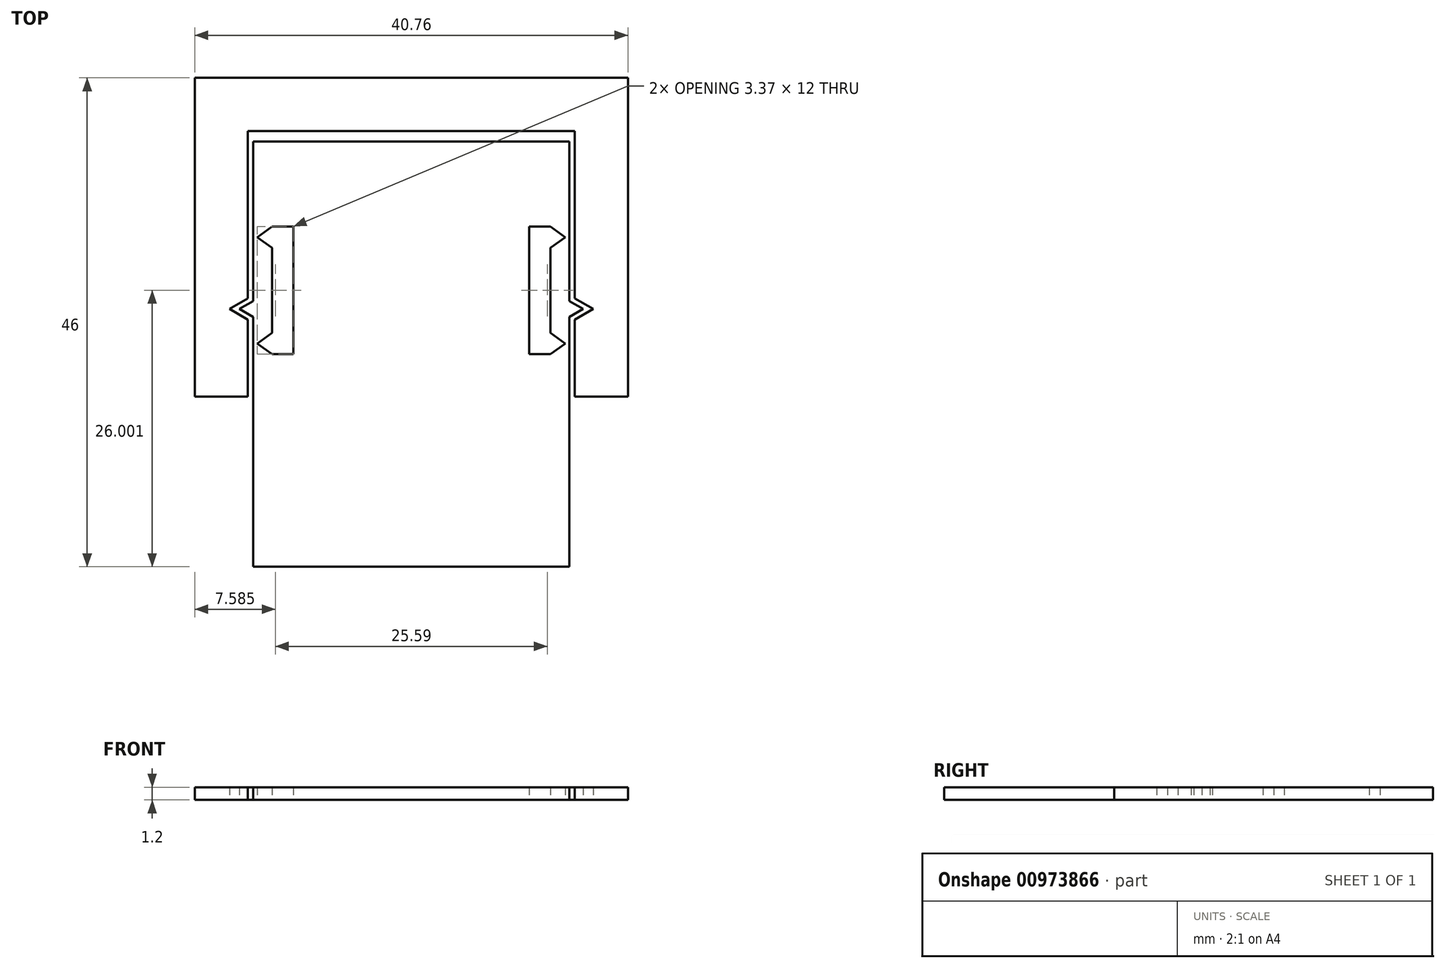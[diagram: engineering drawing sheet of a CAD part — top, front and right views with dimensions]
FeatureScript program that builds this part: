
annotation { "Feature Type Name" : "Feature", "Feature Type Description" : "" }
export const myFeature = defineFeature(function(context is Context, id is Id, definition is map)
    precondition{}
    {
        {
            var Q0;
            Q0=qCreatedBy(makeId("Top.planeOp"),FACE);
            var sketch = newSketch(context, id + "F0", { "sketchPlane" : qUnion([Q0])});
            skPoint(sketch, "E0.middle", {"position": v(0.12, -0.08) * mm});
            skLineSegment(sketch, "E1.bottom", {"start": v(-15.38, -4.08) * mm, "end": v(-20.38, -4.08) * mm});
            skLineSegment(sketch, "E1.top", {"start": v(-15.38, 25.92) * mm, "end": v(-20.38, 25.92) * mm});
            skLineSegment(sketch, "E1.right", {"start": v(-20.38, -4.08) * mm, "end": v(-20.38, 25.92) * mm});
            skLineSegment(sketch, "E2.left", {"start": v(-15.38, 25.92) * mm, "end": v(-15.38, 20.92) * mm});
            skLineSegment(sketch, "E3.bottom", {"start": v(-13.1, 11.92) * mm, "end": v(-11.1, 11.92) * mm});
            skLineSegment(sketch, "E3.top", {"start": v(-13.1, -0.08) * mm, "end": v(-11.1, -0.08) * mm});
            skLineSegment(sketch, "E3.right", {"start": v(-11.1, 11.92) * mm, "end": v(-11.1, -0.08) * mm});
            skLineSegment(sketch, "E4", {"start": v(-13.1, 9.92) * mm, "end": v(-14.48, 10.92) * mm});
            skLineSegment(sketch, "E5", {"start": v(-14.48, 10.92) * mm, "end": v(-13.1, 11.92) * mm});
            skLineSegment(sketch, "E6", {"start": v(-13.1, -0.08) * mm, "end": v(-14.48, 0.92) * mm});
            skLineSegment(sketch, "E7", {"start": v(-14.48, 0.92) * mm, "end": v(-13.1, 1.92) * mm});
            skLineSegment(sketch, "E8", {"start": v(-13.1, 9.92) * mm, "end": v(-13.1, 1.92) * mm});
            skLineSegment(sketch, "E9", {"start": v(-14.88, 3.42) * mm, "end": v(-16.18, 4.17) * mm});
            skLineSegment(sketch, "E10", {"start": v(-16.18, 4.17) * mm, "end": v(-14.88, 4.92) * mm});
            skLineSegment(sketch, "E11", {"start": v(-15.38, 5.17) * mm, "end": v(-17.12, 4.17) * mm});
            skLineSegment(sketch, "E12", {"start": v(-17.12, 4.17) * mm, "end": v(-15.38, 3.17) * mm});
            skLineSegment(sketch, "E13", {"start": v(-15.38, -4.08) * mm, "end": v(-15.38, 3.17) * mm});
            skLineSegment(sketch, "E14", {"start": v(-15.38, 5.17) * mm, "end": v(-15.38, 20.92) * mm});
            skLineSegment(sketch, "E15", {"start": v(-14.88, 3.42) * mm, "end": v(-14.88, -20.08) * mm});
            skLineSegment(sketch, "E16", {"start": v(-14.88, 4.92) * mm, "end": v(-14.88, 19.92) * mm});
            skLineSegment(sketch, "E17", {"start": v(0, 29.14) * mm, "end": v(0, -29.34) * mm});
            skLineSegment(sketch, "E18", {"start": v(-15.38, 25.92) * mm, "end": v(0, 25.92) * mm});
            skLineSegment(sketch, "E19", {"start": v(-15.38, 20.92) * mm, "end": v(0, 20.92) * mm});
            skLineSegment(sketch, "E20", {"start": v(-14.88, 19.92) * mm, "end": v(0, 19.92) * mm});
            skLineSegment(sketch, "E21", {"start": v(-14.88, -20.08) * mm, "end": v(0, -20.08) * mm});
            skLineSegment(sketch, "E22.MirrorCS", {"start": v(17.12, 4.17) * mm, "end": v(15.38, 3.17) * mm});
            skLineSegment(sketch, "E23.MirrorCS", {"start": v(14.88, 3.42) * mm, "end": v(16.18, 4.17) * mm});
            skLineSegment(sketch, "E24.MirrorCS", {"start": v(13.1, -0.08) * mm, "end": v(14.48, 0.92) * mm});
            skLineSegment(sketch, "E25.MirrorCS", {"start": v(13.1, 9.92) * mm, "end": v(14.48, 10.92) * mm});
            skLineSegment(sketch, "E26.MirrorCS", {"start": v(14.48, 10.92) * mm, "end": v(13.1, 11.92) * mm});
            skLineSegment(sketch, "E27.MirrorCS", {"start": v(14.48, 0.92) * mm, "end": v(13.1, 1.92) * mm});
            skLineSegment(sketch, "E28.MirrorCS", {"start": v(13.1, 11.92) * mm, "end": v(11.1, 11.92) * mm});
            skLineSegment(sketch, "E29.MirrorCS", {"start": v(15.38, 5.17) * mm, "end": v(17.12, 4.17) * mm});
            skLineSegment(sketch, "E30.MirrorCS", {"start": v(16.18, 4.17) * mm, "end": v(14.88, 4.92) * mm});
            skLineSegment(sketch, "E31.MirrorCS", {"start": v(13.1, -0.08) * mm, "end": v(11.1, -0.08) * mm});
            skLineSegment(sketch, "E32.MirrorCS", {"start": v(11.1, 11.92) * mm, "end": v(11.1, -0.08) * mm});
            skLineSegment(sketch, "E33.MirrorCS", {"start": v(15.38, 25.92) * mm, "end": v(0, 25.92) * mm});
            skLineSegment(sketch, "E34.MirrorCS", {"start": v(15.38, 20.92) * mm, "end": v(0, 20.92) * mm});
            skLineSegment(sketch, "E35.MirrorCS", {"start": v(15.38, 25.92) * mm, "end": v(15.38, 20.92) * mm});
            skLineSegment(sketch, "E36.MirrorCS", {"start": v(15.38, 25.92) * mm, "end": v(20.38, 25.92) * mm});
            skLineSegment(sketch, "E37.MirrorCS", {"start": v(14.88, 4.92) * mm, "end": v(14.88, 19.92) * mm});
            skLineSegment(sketch, "E38.MirrorCS", {"start": v(15.38, 5.17) * mm, "end": v(15.38, 20.92) * mm});
            skLineSegment(sketch, "E39.MirrorCS", {"start": v(15.38, -4.08) * mm, "end": v(20.38, -4.08) * mm});
            skLineSegment(sketch, "E40.MirrorCS", {"start": v(13.1, 9.92) * mm, "end": v(13.1, 1.92) * mm});
            skLineSegment(sketch, "E41.MirrorCS", {"start": v(20.38, -4.08) * mm, "end": v(20.38, 25.92) * mm});
            skLineSegment(sketch, "E42.MirrorCS", {"start": v(14.88, 19.92) * mm, "end": v(0, 19.92) * mm});
            skLineSegment(sketch, "E43.MirrorCS", {"start": v(15.38, -4.08) * mm, "end": v(15.38, 3.17) * mm});
            skLineSegment(sketch, "E44.MirrorCS", {"start": v(14.88, 3.42) * mm, "end": v(14.88, -20.08) * mm});
            skLineSegment(sketch, "E45.MirrorCS", {"start": v(14.88, -20.08) * mm, "end": v(0, -20.08) * mm});
            skSolve(sketch);
        }
        {
            var Q0;
            Q0=makeQuery(id+"F0.imprint","IMPRINT",FACE,{"disambiguationData":[TD([[makeQuery(id+"F0.imprint","IMPRINT",EDGE,{"derivedFrom":sQuery(id+"F0.wireOp",EDGE,"E23.MirrorCS")}),1.0]])]});
            var Q1;
            Q1=makeQuery(id+"F0.imprint","IMPRINT",FACE,{"disambiguationData":[TD([[makeQuery(id+"F0.imprint","IMPRINT",EDGE,{"derivedFrom":sQuery(id+"F0.wireOp",EDGE,"E3.bottom")}),1.0]])]});
            var Q2;
            Q2=makeQuery(id+"F0.imprint","IMPRINT",FACE,{"disambiguationData":[TD([[makeQuery(id+"F0.imprint","IMPRINT",EDGE,{"derivedFrom":sQuery(id+"F0.wireOp",EDGE,"E1.bottom")}),-1.0]])]});
            var Q3;
            Q3=makeQuery(id+"F0.imprint","IMPRINT",FACE,{"disambiguationData":[TD([[makeQuery(id+"F0.imprint","IMPRINT",EDGE,{"derivedFrom":sQuery(id+"F0.wireOp",EDGE,"E2.left")}),1.0]])]});
            var Q4;
            Q4=makeQuery(id+"F0.imprint","IMPRINT",FACE,{"disambiguationData":[TD([[makeQuery(id+"F0.imprint","IMPRINT",EDGE,{"derivedFrom":sQuery(id+"F0.wireOp",EDGE,"E22.MirrorCS")}),1.0]])]});
            var Q5;
            {var subQ0=sQuery(id+"F0.wireOp",EDGE,"E33.MirrorCS");Q5=makeQuery(id+"F0.imprint","IMPRINT",FACE,{"disambiguationData":[TD([[makeQuery(id+"F0.imprint","IMPRINT",EDGE,{"derivedFrom":subQ0}),1.0]])]});}
            extrude(context, id + "F1", {"entities" : qUnion([Q0, Q1, Q2, Q3, Q4, Q5]), "depth" : 1.2 * mm, "offsetDistance" : 25 * mm});
        }
    });
